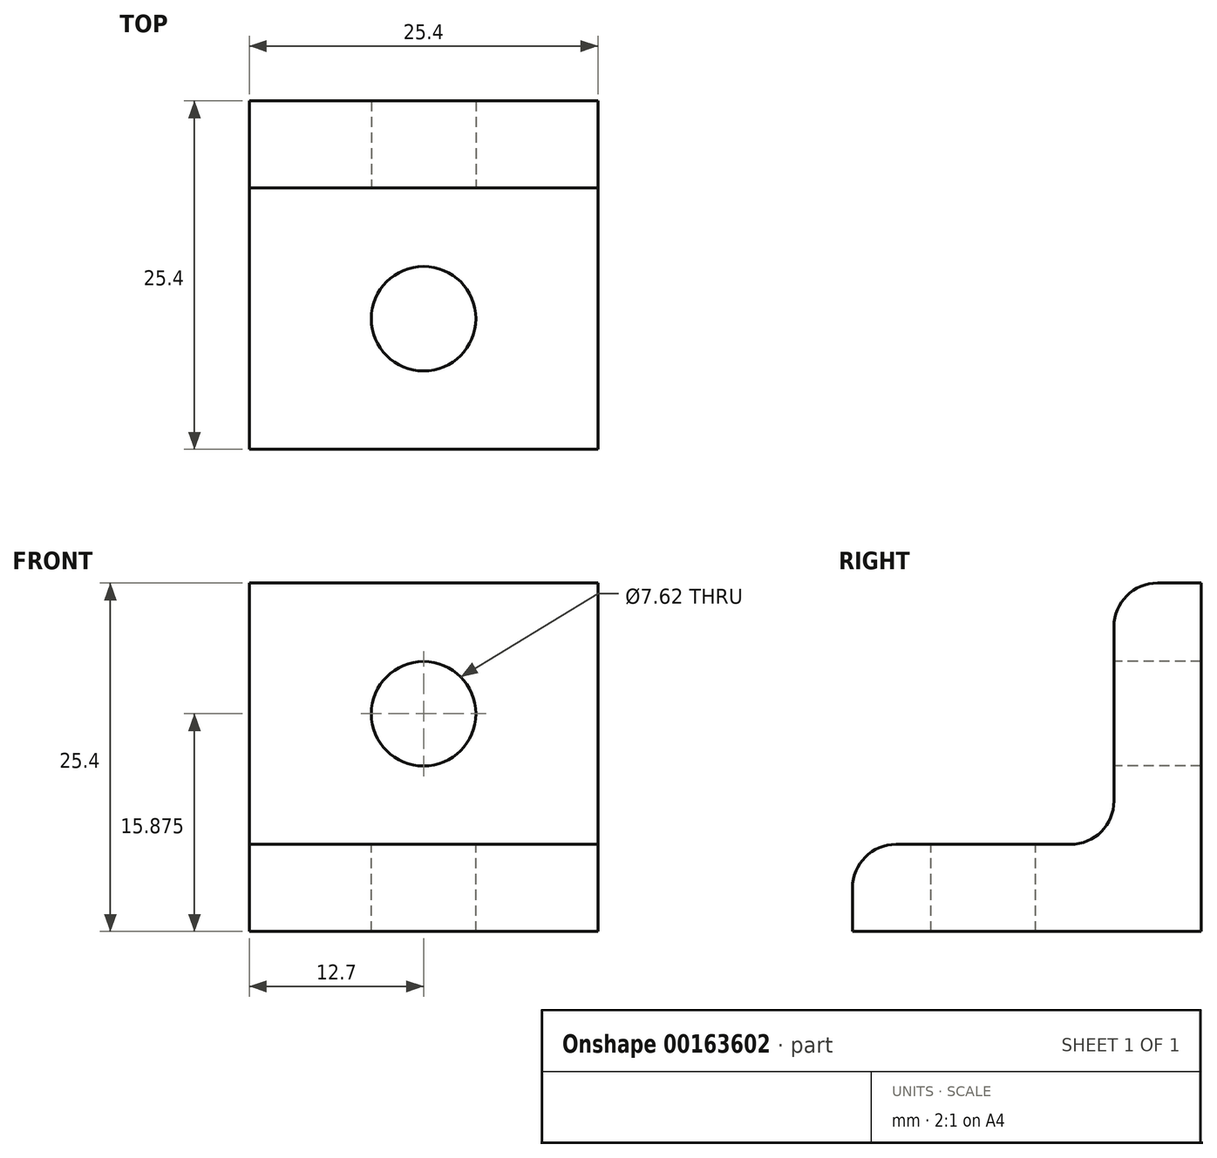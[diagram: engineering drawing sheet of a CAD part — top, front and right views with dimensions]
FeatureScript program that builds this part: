
annotation { "Feature Type Name" : "Feature", "Feature Type Description" : "" }
export const myFeature = defineFeature(function(context is Context, id is Id, definition is map)
    precondition{}
    {
        {
            var Q0;
            Q0=qCreatedBy(makeId("Right.planeOp"),FACE);
            var sketch = newSketch(context, id + "F0", { "sketchPlane" : qUnion([Q0])});
            skLineSegment(sketch, "E0", {"start": v(0, 0) * mm, "end": v(25.4, 0) * mm});
            skLineSegment(sketch, "E1", {"start": v(25.4, 0) * mm, "end": v(25.4, 25.4) * mm});
            skLineSegment(sketch, "E2", {"start": v(25.4, 25.4) * mm, "end": v(19.05, 25.4) * mm});
            skLineSegment(sketch, "E3", {"start": v(19.05, 25.4) * mm, "end": v(19.05, 6.35) * mm});
            skLineSegment(sketch, "E4", {"start": v(19.05, 6.35) * mm, "end": v(0, 6.35) * mm});
            skLineSegment(sketch, "E5", {"start": v(0, 6.35) * mm, "end": v(0, 0) * mm});
            skSolve(sketch);
        }
        {
            var Q0;
            Q0 = qSketchRegion(id + "F0", true);
            extrude(context, id + "F1", {"entities" : qUnion([Q0]), "endBound" : BoundingType.SYMMETRIC, "depth" : 25.4 * mm});
        }
        {
            var Q0;
            Q0=makeQuery(id+"F1.opExtrude","SWEPT_EDGE",EDGE,{"disambiguationData":[OSD([sQuery(id+"F0.wireOp",EDGE,"E4"),sQuery(id+"F0.wireOp",EDGE,"E5")])]});
            var Q1;
            Q1=makeQuery(id+"F1.opExtrude","SWEPT_EDGE",EDGE,{"disambiguationData":[OSD([sQuery(id+"F0.wireOp",EDGE,"E3"),sQuery(id+"F0.wireOp",EDGE,"E4")])]});
            var Q2;
            Q2=makeQuery(id+"F1.opExtrude","SWEPT_EDGE",EDGE,{"disambiguationData":[OSD([sQuery(id+"F0.wireOp",EDGE,"E2"),sQuery(id+"F0.wireOp",EDGE,"E3")])]});
            fillet(context, id + "F2", {"entities" : qUnion([Q0, Q1, Q2]), "radius" : 3.17 * mm, "tangentPropagation" : true, "allowEdgeOverflow" : false});
        }
        {
            var Q0;
            Q0=makeQuery(id+"F1.opExtrude","SWEPT_FACE",FACE,{"disambiguationData":[OSD([sQuery(id+"F0.wireOp",EDGE,"E4")])]});
            var sketch = newSketch(context, id + "F3", { "sketchPlane" : qUnion([Q0])});
            skCircle(sketch, "E6", {"center": v(0, 9.52) * mm, "radius": 3.81 * mm});
            skPoint(sketch, "E6.centerSnap0", {"position": v(-12.7, 9.52) * mm});
            skSolve(sketch);
        }
        {
            var Q0;
            Q0 = qSketchRegion(id + "F3", true);
            extrude(context, id + "F4", {"entities" : qUnion([Q0]), "operationType" : NewBodyOperationType.REMOVE, "oppositeDirection" : true, "depth" : 25.4 * mm});
        }
        {
            var Q0;
            Q0=makeQuery(id+"F1.opExtrude","SWEPT_FACE",FACE,{"disambiguationData":[OSD([sQuery(id+"F0.wireOp",EDGE,"E3")])]});
            var sketch = newSketch(context, id + "F5", { "sketchPlane" : qUnion([Q0])});
            skCircle(sketch, "E7", {"center": v(0, 15.88) * mm, "radius": 3.81 * mm});
            skPoint(sketch, "E7.centerSnap0", {"position": v(-12.7, 15.88) * mm});
            skPoint(sketch, "E7.centerSnap1", {"position": v(0, 9.53) * mm});
            skSolve(sketch);
        }
        {
            var Q0;
            Q0 = qSketchRegion(id + "F5", true);
            extrude(context, id + "F6", {"entities" : qUnion([Q0]), "operationType" : NewBodyOperationType.REMOVE, "oppositeDirection" : true, "depth" : 25.4 * mm});
        }
    });
